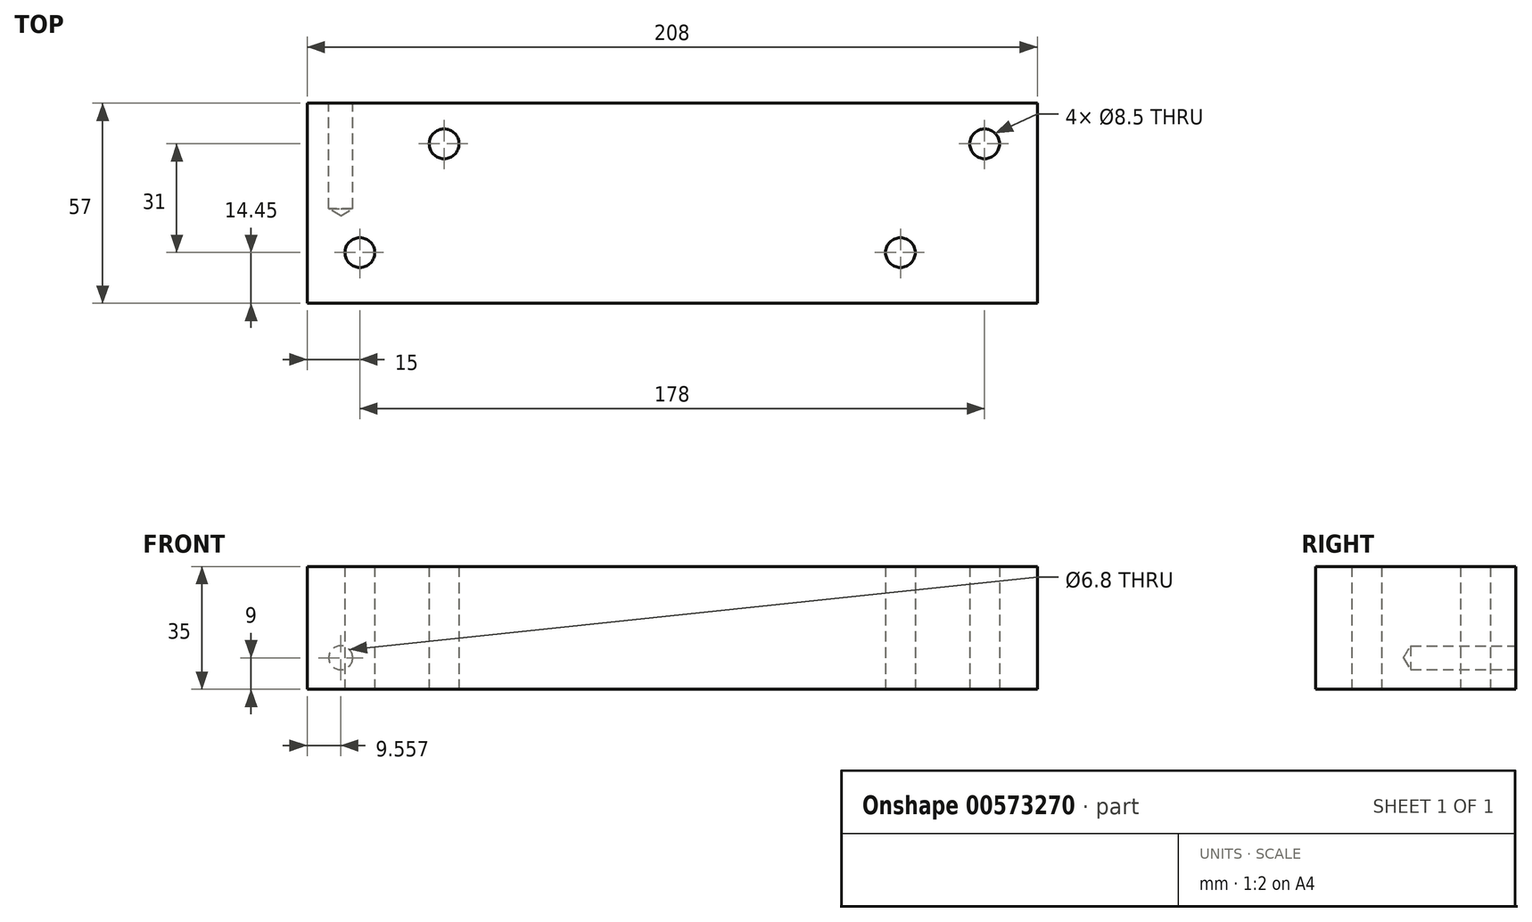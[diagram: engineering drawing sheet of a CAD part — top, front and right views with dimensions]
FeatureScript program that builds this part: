
annotation { "Feature Type Name" : "Feature", "Feature Type Description" : "" }
export const myFeature = defineFeature(function(context is Context, id is Id, definition is map)
    precondition{}
    {
        {
            var Q0;
            Q0=qCreatedBy(makeId("Top.planeOp"),FACE);
            var sketch = newSketch(context, id + "F0", { "sketchPlane" : qUnion([Q0])});
            skLineSegment(sketch, "E0.bottom", {"start": v(0, 0) * mm, "end": v(208, 0) * mm});
            skLineSegment(sketch, "E0.top", {"start": v(0, 57) * mm, "end": v(208, 57) * mm});
            skLineSegment(sketch, "E0.left", {"start": v(0, 0) * mm, "end": v(0, 57) * mm});
            skLineSegment(sketch, "E0.right", {"start": v(208, 0) * mm, "end": v(208, 57) * mm});
            skPoint(sketch, "E1", {"position": v(39, 45.45) * mm});
            skPoint(sketch, "E2", {"position": v(193, 45.45) * mm});
            skPoint(sketch, "E3", {"position": v(169, 14.45) * mm});
            skPoint(sketch, "E4", {"position": v(15, 14.45) * mm});
            skSolve(sketch);
        }
        {
            var Q0;
            Q0 = qSketchRegion(id + "F0", true);
            extrude(context, id + "F1", {"entities" : qUnion([Q0]), "depth" : 35 * mm, "offsetDistance" : 25 * mm});
        }
        {
            var Q0;
            Q0=makeQuery(id+"F1.opExtrude","SWEPT_FACE",FACE,{"disambiguationData":[OSD([sQuery(id+"F0.wireOp",EDGE,"E0.top")])]});
            var sketch = newSketch(context, id + "F2", { "sketchPlane" : qUnion([Q0])});
            skPoint(sketch, "E5", {"position": v(-9.56, 9) * mm});
            skSolve(sketch);
        }
        {
            var Q0;
            Q0=sQuery(id+"F2.wireOp",VERTEX,"E5");
            var Q1;
            Q1=makeQuery(id+"F1.opExtrude","SWEPT_BODY",BODY,{"disambiguationData":[OSD([sQuery(id+"F0.wireOp",EDGE,"E0.bottom"),sQuery(id+"F0.wireOp",EDGE,"E0.top"),sQuery(id+"F0.wireOp",EDGE,"E0.left"),sQuery(id+"F0.wireOp",EDGE,"E0.right"),sQuery(id+"F0.wireOp",EDGE,"2yPMVlZM-9zrR-AzKY-Udva-lTU6px8fucxC"),sQuery(id+"F0.wireOp",EDGE,"JVjqsgh5-bqWj-ADOh-1Cvm-CDBHs16gkmBc"),sQuery(id+"F0.wireOp",EDGE,"VkgpQDv8-SMyc-Bcih-KuVh-fFp9XhJGBaqj"),sQuery(id+"F0.wireOp",EDGE,"0Wq6xl8I-RJnE-96rY-kfQZ-TPv4l3mD2TAt")])]});
            hole(context, id + "F3", {"style" : HoleStyle.SIMPLE, "endStyle" : HoleEndStyle.BLIND, "standardTappedOrClearance" : lookupTablePath({ "standard" : "ISO", "engagement" : "75%", "pitch" : "1.25 mm", "size" : "M8", "type" : "Tapped" }), "standardBlindInLast" : lookupTablePath({ "standard" : "ISO", "engagement" : "75%", "pitch" : "1.25 mm", "size" : "M8", "type" : "Tapped" }), "holeDiameter" : 6.8 * mm, "showTappedDepth" : true, "holeDepth" : 30 * mm, "tappedDepth" : 26.25 * mm, "tapClearance" : 3, "locations" : qUnion([Q0]), "scope" : qUnion([Q1]), "majorDiameter" : 8 * mm});
        }
        {
            var Q0;
            Q0=sQuery(id+"F0.wireOp",VERTEX,"E2");
            var Q1;
            Q1=sQuery(id+"F0.wireOp",VERTEX,"E3");
            var Q2;
            Q2=sQuery(id+"F0.wireOp",VERTEX,"E1");
            var Q3;
            Q3=sQuery(id+"F0.wireOp",VERTEX,"E4");
            var Q4;
            Q4=makeQuery(id+"F1.opExtrude","SWEPT_BODY",BODY,{"disambiguationData":[OSD([sQuery(id+"F0.wireOp",EDGE,"E0.bottom"),sQuery(id+"F0.wireOp",EDGE,"E0.top"),sQuery(id+"F0.wireOp",EDGE,"E0.left"),sQuery(id+"F0.wireOp",EDGE,"E0.right")])]});
            hole(context, id + "F4", {"style" : HoleStyle.SIMPLE, "endStyle" : HoleEndStyle.THROUGH, "oppositeDirection" : true, "standardTappedOrClearance" : lookupTablePath({ "standard" : "ISO", "engagement" : "75%", "pitch" : "1.5 mm", "size" : "M10", "type" : "Tapped" }), "standardBlindInLast" : lookupTablePath({ "standard" : "ISO", "engagement" : "75%", "pitch" : "1.5 mm", "size" : "M10", "type" : "Tapped" }), "holeDiameter" : 8.5 * mm, "showTappedDepth" : true, "isTappedThrough" : true, "tappedDepth" : 12 * mm, "tapClearance" : 3, "locations" : qUnion([Q0, Q1, Q2, Q3]), "scope" : qUnion([Q4]), "majorDiameter" : 10 * mm});
        }
    });
